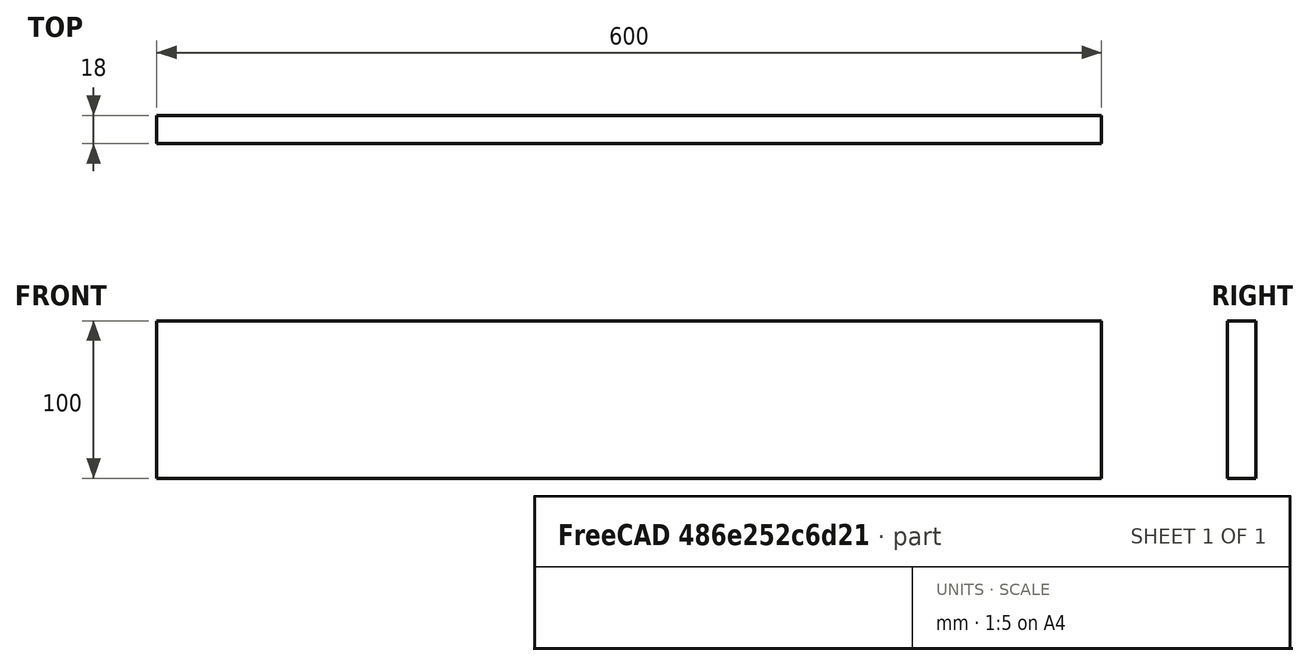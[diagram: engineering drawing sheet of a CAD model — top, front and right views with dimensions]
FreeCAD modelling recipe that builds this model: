
FCSTD DOCUMENT  (FreeCAD 0.18R4 (GitTag))
Label: small_back
License: All rights reserved
LicenseURL: http://en.wikipedia.org/wiki/All_rights_reserved
objects: Sketcher::SketchObject×1, PartDesign::Pad×1, PartDesign::Body×1
note: 4 computed .brp shape members not serialized (recipe doc carries the construction recipe); baked Part::Feature solids carry a one-line shape summary decoded from their .brp

FEATURE [Sketcher::SketchObject] Sketch
  MapMode = 5
  Placement = pos=(0,0,0) rot=(1,0,0;1.5708rad)
  Support = -> [XZ_Plane]
  sketch-geometry (4):
    g0: LineSegment StartX=0 StartY=0 StartZ=0 EndX=-600 EndY=0 EndZ=0
    g1: LineSegment StartX=-600 StartY=0 StartZ=0 EndX=-600 EndY=100 EndZ=0
    g2: LineSegment StartX=-600 StartY=100 StartZ=0 EndX=0 EndY=100 EndZ=0
    g3: LineSegment StartX=0 StartY=100 StartZ=0 EndX=0 EndY=0 EndZ=0
  constraints (11):
    c: Coincident(g0,g1)
    c: Coincident(g1,g2)
    c: Coincident(g2,g3)
    c: Coincident(g3,g0)
    c: Horizontal(g0)
    c: Horizontal(g2)
    c: Vertical(g1)
    c: Vertical(g3)
    c: Coincident(g0,g-1)
    c: DistanceY(g3,g3) = 100
    c: DistanceX(g0,g0) = 600
FEATURE [PartDesign::Pad] Pad
  Length = 18
  Length2 = 100
  Placement = pos=(0,0,0) rot=(1,0,0;1.5708rad)
  Profile = -> Sketch
  Type = 0
FEATURE [PartDesign::Body] Body
  Group = -> [Sketch,Pad]
  Origin = -> Origin
  Tip = -> Pad
